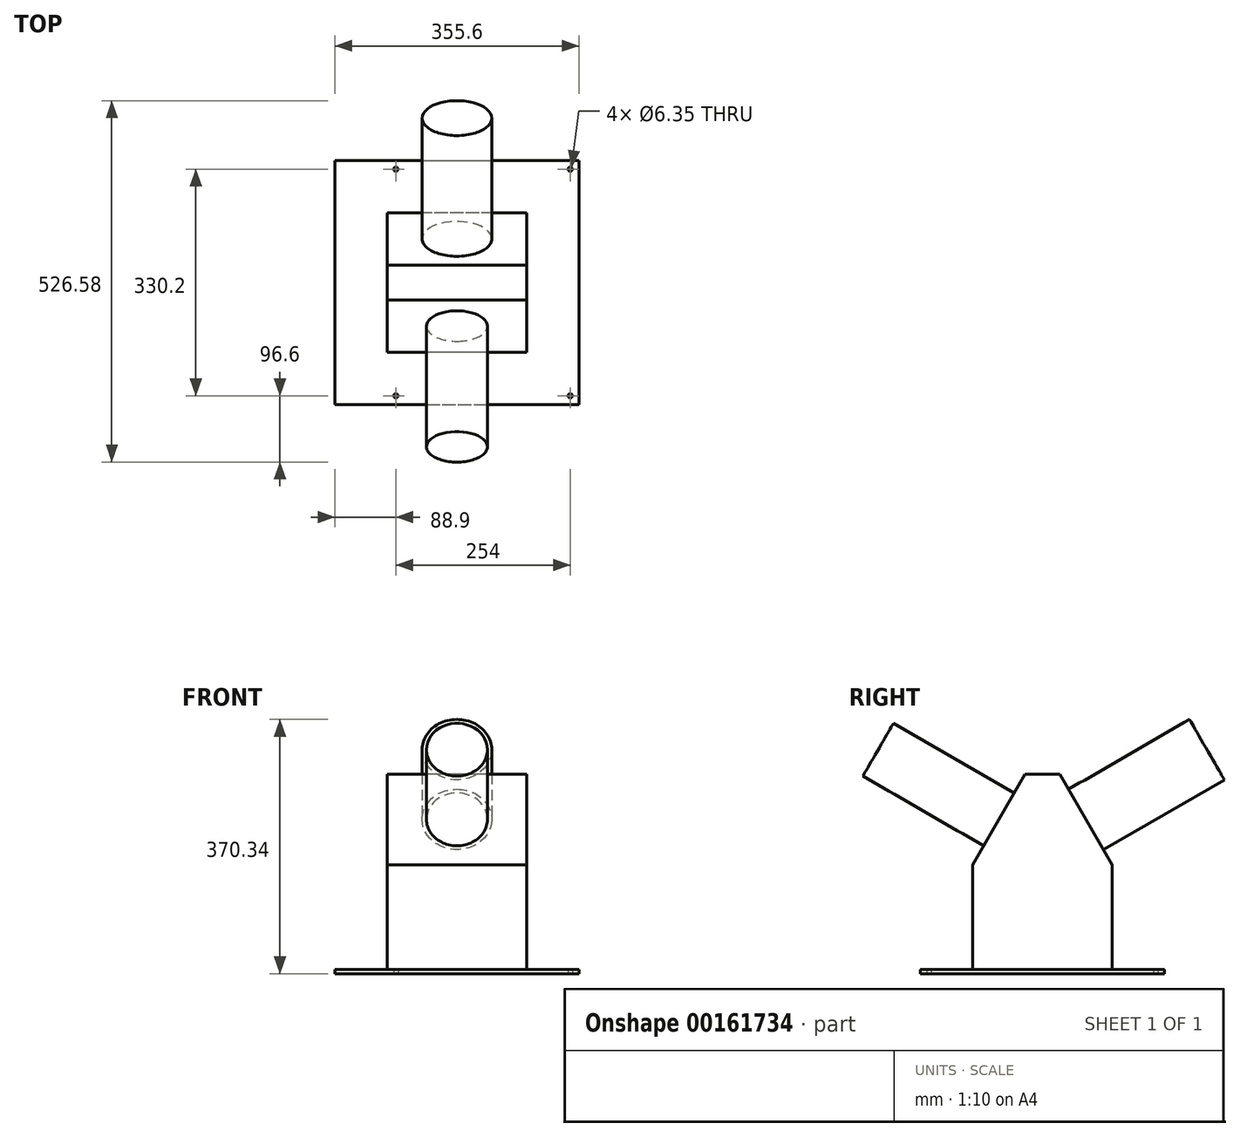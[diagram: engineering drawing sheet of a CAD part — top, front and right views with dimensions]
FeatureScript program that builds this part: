
annotation { "Feature Type Name" : "Feature", "Feature Type Description" : "" }
export const myFeature = defineFeature(function(context is Context, id is Id, definition is map)
    precondition{}
    {
        {
            var Q0;
            Q0=qCreatedBy(makeId("Right.planeOp"),FACE);
            var sketch = newSketch(context, id + "F0", { "sketchPlane" : qUnion([Q0])});
            skLineSegment(sketch, "E0", {"start": v(-101.6, 0) * mm, "end": v(101.6, 0) * mm});
            skLineSegment(sketch, "E1", {"start": v(101.6, 0) * mm, "end": v(101.6, 152.4) * mm});
            skLineSegment(sketch, "E2", {"start": v(101.6, 152.4) * mm, "end": v(25.4, 284.38) * mm});
            skLineSegment(sketch, "E3", {"start": v(25.4, 284.38) * mm, "end": v(-25.4, 284.38) * mm});
            skLineSegment(sketch, "E4", {"start": v(-25.4, 284.38) * mm, "end": v(-101.6, 152.4) * mm});
            skLineSegment(sketch, "E5", {"start": v(-101.6, 152.4) * mm, "end": v(-101.6, 0) * mm});
            skSolve(sketch);
        }
        {
            var Q0;
            Q0 = qSketchRegion(id + "F0", true);
            extrude(context, id + "F1", {"entities" : qUnion([Q0]), "depth" : 203.2 * mm});
        }
        {
            var Q0;
            Q0=makeQuery(id+"F1.opExtrude","SWEPT_FACE",FACE,{"disambiguationData":[OSD([sQuery(id+"F0.wireOp",EDGE,"E2")])]});
            var sketch = newSketch(context, id + "F2", { "sketchPlane" : qUnion([Q0])});
            skCircle(sketch, "E6", {"center": v(-101.6, 157.38) * mm, "radius": 50.8 * mm});
            skPoint(sketch, "E6.centerSnap0", {"position": v(-203.2, 157.38) * mm});
            skPoint(sketch, "E6.centerSnap1", {"position": v(-101.6, 233.58) * mm});
            skSolve(sketch);
        }
        {
            var Q0;
            Q0 = qSketchRegion(id + "F2", true);
            extrude(context, id + "F3", {"entities" : qUnion([Q0]), "operationType" : NewBodyOperationType.ADD, "depth" : 203.2 * mm});
        }
        {
            var Q0;
            Q0=makeQuery(id+"F1.opExtrude","SWEPT_FACE",FACE,{"disambiguationData":[OSD([sQuery(id+"F0.wireOp",EDGE,"E4")])]});
            var sketch = newSketch(context, id + "F4", { "sketchPlane" : qUnion([Q0])});
            skCircle(sketch, "E7", {"center": v(101.6, 157.38) * mm, "radius": 44.45 * mm});
            skPoint(sketch, "E7.centerSnap0", {"position": v(0, 157.38) * mm});
            skPoint(sketch, "E7.centerSnap1", {"position": v(101.6, 233.58) * mm});
            skSolve(sketch);
        }
        {
            var Q0;
            Q0 = qSketchRegion(id + "F4", true);
            extrude(context, id + "F5", {"entities" : qUnion([Q0]), "operationType" : NewBodyOperationType.ADD, "depth" : 203.2 * mm});
        }
        {
            var Q0;
            Q0=makeQuery(id+"F1.opExtrude","SWEPT_FACE",FACE,{"disambiguationData":[OSD([sQuery(id+"F0.wireOp",EDGE,"E0")])]});
            var sketch = newSketch(context, id + "F6", { "sketchPlane" : qUnion([Q0])});
            skLineSegment(sketch, "E8.bottom", {"start": v(-76.2, 177.8) * mm, "end": v(279.4, 177.8) * mm});
            skLineSegment(sketch, "E8.top", {"start": v(-76.2, -177.8) * mm, "end": v(279.4, -177.8) * mm});
            skLineSegment(sketch, "E8.left", {"start": v(-76.2, 177.8) * mm, "end": v(-76.2, -177.8) * mm});
            skLineSegment(sketch, "E8.right", {"start": v(279.4, 177.8) * mm, "end": v(279.4, -177.8) * mm});
            skSolve(sketch);
        }
        {
            var Q0;
            Q0 = qSketchRegion(id + "F6", true);
            extrude(context, id + "F7", {"entities" : qUnion([Q0]), "operationType" : NewBodyOperationType.ADD, "depth" : 6.35 * mm});
        }
        {
            var Q0;
            Q0=makeQuery(id+"F7.opExtrude","CAP_FACE",FACE,{"disambiguationData":[OSD([sQuery(id+"F6.wireOp",EDGE,"E8.bottom"),sQuery(id+"F6.wireOp",EDGE,"E8.top"),sQuery(id+"F6.wireOp",EDGE,"E8.left"),sQuery(id+"F6.wireOp",EDGE,"E8.right")])],"isStart":false});
            var sketch = newSketch(context, id + "F8", { "sketchPlane" : qUnion([Q0])});
            skCircle(sketch, "E9", {"center": v(266.7, 165.1) * mm, "radius": 3.18 * mm});
            skCircle(sketch, "E10", {"center": v(266.7, -165.1) * mm, "radius": 3.18 * mm});
            skCircle(sketch, "E11", {"center": v(12.7, -165.1) * mm, "radius": 3.18 * mm});
            skCircle(sketch, "E12", {"center": v(12.7, 165.1) * mm, "radius": 3.18 * mm});
            skSolve(sketch);
        }
        {
            var Q0;
            Q0 = qSketchRegion(id + "F8", true);
            var Q1;
            Q1=makeQuery(id+"F7.opExtrude","CAP_FACE",FACE,{"disambiguationData":[OSD([sQuery(id+"F6.wireOp",EDGE,"E8.bottom"),sQuery(id+"F6.wireOp",EDGE,"E8.top"),sQuery(id+"F6.wireOp",EDGE,"E8.left"),sQuery(id+"F6.wireOp",EDGE,"E8.right")])],"isStart":true});
            extrude(context, id + "F9", {"entities" : qUnion([Q0]), "operationType" : NewBodyOperationType.REMOVE, "endBound" : BoundingType.UP_TO_SURFACE, "oppositeDirection" : true, "endBoundEntityFace" : qUnion([Q1]), "depth" : 25.4 * mm});
        }
    });
